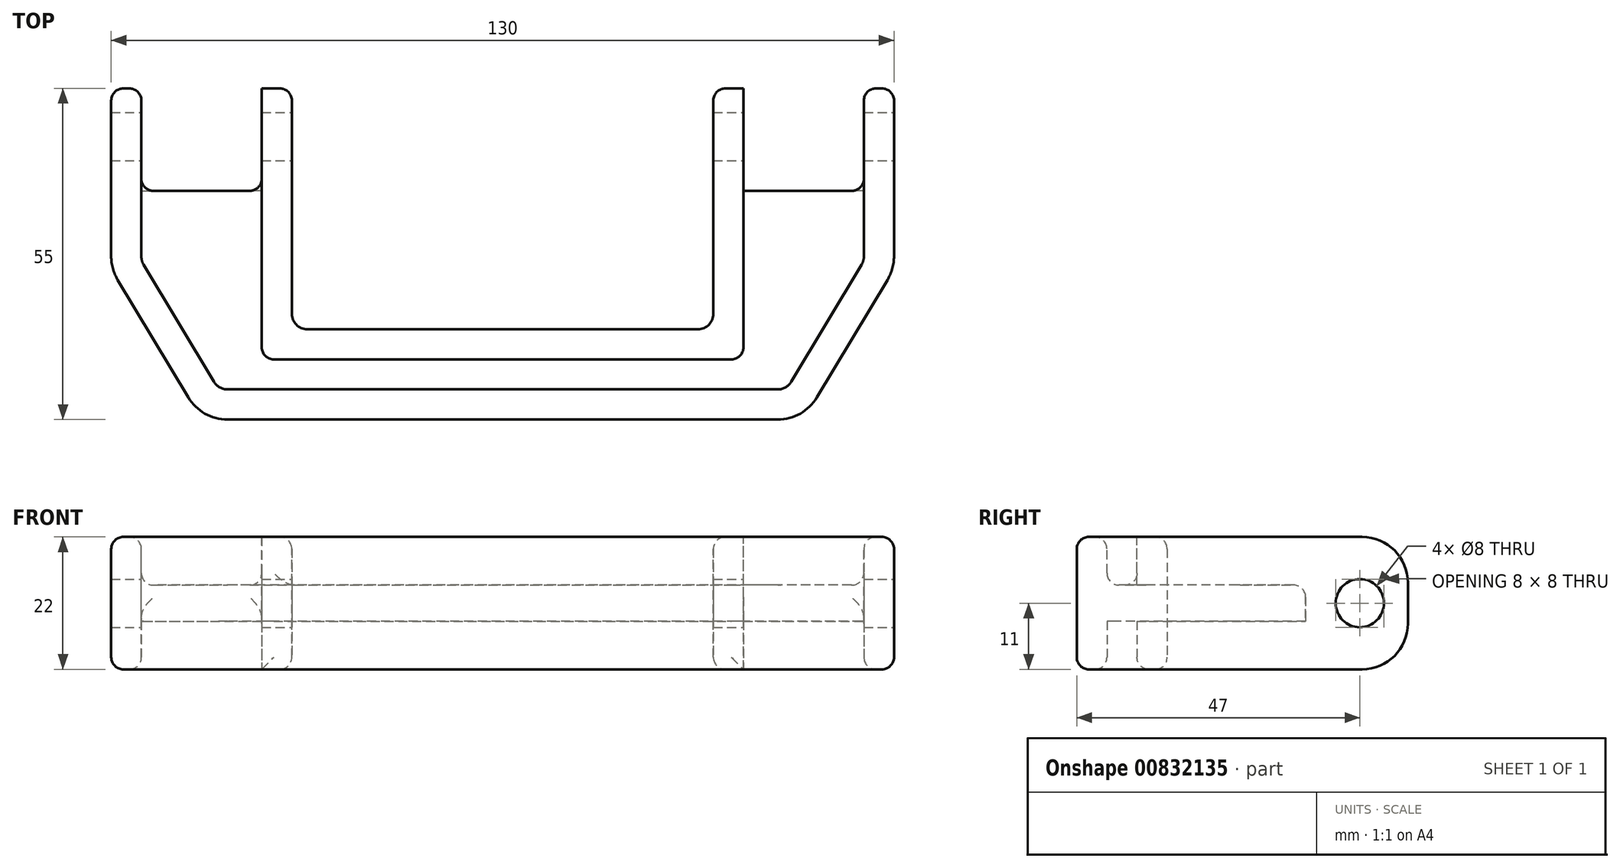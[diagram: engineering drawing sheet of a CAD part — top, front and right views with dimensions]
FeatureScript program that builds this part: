
annotation { "Feature Type Name" : "Feature", "Feature Type Description" : "" }
export const myFeature = defineFeature(function(context is Context, id is Id, definition is map)
    precondition{}
    {
        {
            var Q0;
            Q0=qCreatedBy(makeId("Top.planeOp"),FACE);
            var sketch = newSketch(context, id + "F0", { "sketchPlane" : qUnion([Q0])});
            skLineSegment(sketch, "E0", {"start": v(-65, 30) * mm, "end": v(-35, 30) * mm});
            skLineSegment(sketch, "E1", {"start": v(-35, 30) * mm, "end": v(-35, -10) * mm});
            skLineSegment(sketch, "E2", {"start": v(0, 0) * mm, "end": v(0, -25) * mm});
            skLineSegment(sketch, "E3", {"start": v(65, 30) * mm, "end": v(35, 30) * mm});
            skLineSegment(sketch, "E4", {"start": v(35, 30) * mm, "end": v(35, -10) * mm});
            skLineSegment(sketch, "E5", {"start": v(-35, -10) * mm, "end": v(35, -10) * mm});
            skLineSegment(sketch, "E6", {"start": v(0, -25) * mm, "end": v(-50, -25) * mm});
            skLineSegment(sketch, "E7", {"start": v(0, -25) * mm, "end": v(50, -25) * mm});
            skLineSegment(sketch, "E8", {"start": v(65, 30) * mm, "end": v(65, 0) * mm});
            skLineSegment(sketch, "E9", {"start": v(65, 0) * mm, "end": v(50, -25) * mm});
            skLineSegment(sketch, "E10", {"start": v(-65, 30) * mm, "end": v(-65, 0) * mm});
            skLineSegment(sketch, "E11", {"start": v(-65, 0) * mm, "end": v(-50, -25) * mm});
            skSolve(sketch);
        }
        {
            var Q0;
            Q0 = qSketchRegion(id + "F0", true);
            extrude(context, id + "F1", {"entities" : qUnion([Q0]), "depth" : 22 * mm, "offsetDistance" : 25.4 * mm});
        }
        {
            var Q0;
            Q0=makeQuery(id+"F1.opExtrude","SWEPT_EDGE",EDGE,{"disambiguationData":[OSD([sQuery(id+"F0.wireOp",EDGE,"E7"),sQuery(id+"F0.wireOp",EDGE,"E9")])]});
            var Q1;
            Q1=makeQuery(id+"F1.opExtrude","SWEPT_EDGE",EDGE,{"disambiguationData":[OSD([sQuery(id+"F0.wireOp",EDGE,"E8"),sQuery(id+"F0.wireOp",EDGE,"E9")])]});
            var Q2;
            Q2=makeQuery(id+"F1.opExtrude","SWEPT_EDGE",EDGE,{"disambiguationData":[OSD([sQuery(id+"F0.wireOp",EDGE,"E6"),sQuery(id+"F0.wireOp",EDGE,"E11")])]});
            var Q3;
            Q3=makeQuery(id+"F1.opExtrude","SWEPT_EDGE",EDGE,{"disambiguationData":[OSD([sQuery(id+"F0.wireOp",EDGE,"E10"),sQuery(id+"F0.wireOp",EDGE,"E11")])]});
            fillet(context, id + "F2", {"entities" : qUnion([Q0, Q1, Q2, Q3]), "radius" : 7.62 * mm, "tangentPropagation" : true, "allowEdgeOverflow" : false});
        }
        {
            var Q0;
            Q0=makeQuery(id+"F1.opExtrude","SWEPT_EDGE",EDGE,{"disambiguationData":[OSD([sQuery(id+"F0.wireOp",EDGE,"E4"),sQuery(id+"F0.wireOp",EDGE,"E5")])]});
            var Q1;
            Q1=makeQuery(id+"F1.opExtrude","SWEPT_EDGE",EDGE,{"disambiguationData":[OSD([sQuery(id+"F0.wireOp",EDGE,"E1"),sQuery(id+"F0.wireOp",EDGE,"E5")])]});
            fillet(context, id + "F3", {"entities" : qUnion([Q0, Q1]), "radius" : 2.54 * mm, "tangentPropagation" : true, "allowEdgeOverflow" : false});
        }
        {
            var Q0;
            Q0=makeQuery(id+"F1.opExtrude","CAP_FACE",FACE,{"disambiguationData":[OSD([sQuery(id+"F0.wireOp",EDGE,"E0"),sQuery(id+"F0.wireOp",EDGE,"E1"),sQuery(id+"F0.wireOp",EDGE,"E3"),sQuery(id+"F0.wireOp",EDGE,"E4"),sQuery(id+"F0.wireOp",EDGE,"E5"),sQuery(id+"F0.wireOp",EDGE,"E6"),sQuery(id+"F0.wireOp",EDGE,"E7"),sQuery(id+"F0.wireOp",EDGE,"E8"),sQuery(id+"F0.wireOp",EDGE,"E9"),sQuery(id+"F0.wireOp",EDGE,"E10"),sQuery(id+"F0.wireOp",EDGE,"E11")])],"isStart":false});
            var sketch = newSketch(context, id + "F4", { "sketchPlane" : qUnion([Q0])});
            skLineSegment(sketch, "E12.1", {"start": v(60, 25) * mm, "end": v(60, 2.11) * mm});
            skArc(sketch, "E12.2", {"start": v(59.63, 0.76) * mm, "mid": v(59.9, 1.41) * mm, "end": v(60, 2.11) * mm});
            skLineSegment(sketch, "E12.3", {"start": v(59.63, 0.76) * mm, "end": v(47.93, -18.73) * mm});
            skArc(sketch, "E12.4", {"start": v(45.69, -20) * mm, "mid": v(46.98, -19.66) * mm, "end": v(47.93, -18.73) * mm});
            skLineSegment(sketch, "E12.5", {"start": v(-40, 25) * mm, "end": v(-40, -7.46) * mm});
            skLineSegment(sketch, "E12.7", {"start": v(-32.46, -15) * mm, "end": v(32.46, -15) * mm});
            skLineSegment(sketch, "E12.10", {"start": v(-60, 25) * mm, "end": v(-60, 2.11) * mm});
            skArc(sketch, "E12.11", {"start": v(-60, 2.11) * mm, "mid": v(-59.9, 1.41) * mm, "end": v(-59.63, 0.76) * mm});
            skLineSegment(sketch, "E12.12", {"start": v(-59.63, 0.76) * mm, "end": v(-47.93, -18.73) * mm});
            skArc(sketch, "E12.13", {"start": v(-47.93, -18.73) * mm, "mid": v(-46.98, -19.66) * mm, "end": v(-45.69, -20) * mm});
            skLineSegment(sketch, "E12.14", {"start": v(40, 25) * mm, "end": v(40, -7.46) * mm});
            skLineSegment(sketch, "E12.15", {"start": v(45.69, -20) * mm, "end": v(-45.69, -20) * mm});
            skLineSegment(sketch, "E13", {"start": v(-40, -7.46) * mm, "end": v(-40, -15) * mm});
            skLineSegment(sketch, "E14", {"start": v(-40, -15) * mm, "end": v(-32.46, -15) * mm});
            skLineSegment(sketch, "E15", {"start": v(32.46, -15) * mm, "end": v(40, -15) * mm});
            skLineSegment(sketch, "E16", {"start": v(40, -15) * mm, "end": v(40, -7.46) * mm});
            skLineSegment(sketch, "E17", {"start": v(40, 25) * mm, "end": v(40, 30) * mm});
            skLineSegment(sketch, "E18", {"start": v(40, 30) * mm, "end": v(60, 30) * mm});
            skLineSegment(sketch, "E19", {"start": v(60, 30) * mm, "end": v(60, 25) * mm});
            skLineSegment(sketch, "E20", {"start": v(-60, 25) * mm, "end": v(-60, 30) * mm});
            skLineSegment(sketch, "E21", {"start": v(-60, 30) * mm, "end": v(-40, 30) * mm});
            skLineSegment(sketch, "E22", {"start": v(-40, 30) * mm, "end": v(-40, 25) * mm});
            skSolve(sketch);
        }
        {
            var Q0;
            Q0=makeQuery(id+"F1.opExtrude","CAP_EDGE",EDGE,{"disambiguationData":[OSD([sQuery(id+"F0.wireOp",EDGE,"E3")])],"isStart":false});
            var Q1;
            Q1=makeQuery(id+"F1.opExtrude","CAP_EDGE",EDGE,{"disambiguationData":[OSD([sQuery(id+"F0.wireOp",EDGE,"E3")])],"isStart":true});
            var Q2;
            Q2=makeQuery(id+"F1.opExtrude","CAP_EDGE",EDGE,{"disambiguationData":[OSD([sQuery(id+"F0.wireOp",EDGE,"E0")])],"isStart":false});
            var Q3;
            Q3=makeQuery(id+"F1.opExtrude","CAP_EDGE",EDGE,{"disambiguationData":[OSD([sQuery(id+"F0.wireOp",EDGE,"E0")])],"isStart":true});
            fillet(context, id + "F5", {"entities" : qUnion([Q0, Q1, Q2, Q3]), "radius" : 7.62 * mm, "tangentPropagation" : true, "allowEdgeOverflow" : false});
        }
        {
            var Q0;
            Q0 = qSketchRegion(id + "F4", true);
            extrude(context, id + "F6", {"entities" : qUnion([Q0]), "operationType" : NewBodyOperationType.REMOVE, "oppositeDirection" : true, "depth" : 8 * mm, "offsetDistance" : 25.4 * mm});
        }
        {
            var Q0;
            Q0=makeQuery(id+"F1.opExtrude","CAP_FACE",FACE,{"disambiguationData":[OSD([sQuery(id+"F0.wireOp",EDGE,"E0"),sQuery(id+"F0.wireOp",EDGE,"E1"),sQuery(id+"F0.wireOp",EDGE,"E3"),sQuery(id+"F0.wireOp",EDGE,"E4"),sQuery(id+"F0.wireOp",EDGE,"E5"),sQuery(id+"F0.wireOp",EDGE,"E6"),sQuery(id+"F0.wireOp",EDGE,"E7"),sQuery(id+"F0.wireOp",EDGE,"E8"),sQuery(id+"F0.wireOp",EDGE,"E9"),sQuery(id+"F0.wireOp",EDGE,"E10"),sQuery(id+"F0.wireOp",EDGE,"E11")])],"isStart":true});
            var sketch = newSketch(context, id + "F7", { "sketchPlane" : qUnion([Q0])});
            skLineSegment(sketch, "E23.0", {"start": v(60, -22.38) * mm, "end": v(60, -2.11) * mm});
            skArc(sketch, "E23.1", {"start": v(60, -2.11) * mm, "mid": v(59.9, -1.41) * mm, "end": v(59.63, -0.76) * mm});
            skLineSegment(sketch, "E23.2", {"start": v(59.63, -0.76) * mm, "end": v(47.93, 18.73) * mm});
            skArc(sketch, "E23.3", {"start": v(47.93, 18.73) * mm, "mid": v(46.98, 19.66) * mm, "end": v(45.69, 20) * mm});
            skLineSegment(sketch, "E23.4", {"start": v(45.69, 20) * mm, "end": v(-45.69, 20) * mm});
            skLineSegment(sketch, "E23.6", {"start": v(-32.46, 15) * mm, "end": v(32.46, 15) * mm});
            skLineSegment(sketch, "E23.8", {"start": v(40, -22.38) * mm, "end": v(40, 7.46) * mm});
            skLineSegment(sketch, "E23.9", {"start": v(-40, -17.38) * mm, "end": v(-40, 7.46) * mm});
            skLineSegment(sketch, "E23.11", {"start": v(-60, -17.38) * mm, "end": v(-60, -2.11) * mm});
            skArc(sketch, "E23.12", {"start": v(-59.63, -0.76) * mm, "mid": v(-59.9, -1.41) * mm, "end": v(-60, -2.11) * mm});
            skLineSegment(sketch, "E23.13", {"start": v(-59.63, -0.76) * mm, "end": v(-47.93, 18.73) * mm});
            skArc(sketch, "E23.14", {"start": v(-45.69, 20) * mm, "mid": v(-46.98, 19.66) * mm, "end": v(-47.93, 18.73) * mm});
            skLineSegment(sketch, "E24", {"start": v(40, 7.46) * mm, "end": v(40, 15) * mm});
            skLineSegment(sketch, "E25", {"start": v(40, 15) * mm, "end": v(32.46, 15) * mm});
            skLineSegment(sketch, "E26", {"start": v(-40, 7.46) * mm, "end": v(-40, 15) * mm});
            skLineSegment(sketch, "E27", {"start": v(-40, 15) * mm, "end": v(-32.46, 15) * mm});
            skLineSegment(sketch, "E28", {"start": v(-40, -17.38) * mm, "end": v(-40, -32.17) * mm});
            skLineSegment(sketch, "E29", {"start": v(-40, -32.17) * mm, "end": v(-60, -32.17) * mm});
            skLineSegment(sketch, "E30", {"start": v(-60, -32.17) * mm, "end": v(-60, -17.38) * mm});
            skLineSegment(sketch, "E31", {"start": v(60, -22.38) * mm, "end": v(60, -34.16) * mm});
            skLineSegment(sketch, "E32", {"start": v(60, -34.16) * mm, "end": v(40, -34.16) * mm});
            skLineSegment(sketch, "E33", {"start": v(40, -34.16) * mm, "end": v(40, -22.38) * mm});
            skSolve(sketch);
        }
        {
            var Q0;
            Q0 = qSketchRegion(id + "F7", true);
            extrude(context, id + "F8", {"entities" : qUnion([Q0]), "operationType" : NewBodyOperationType.REMOVE, "oppositeDirection" : true, "depth" : 8 * mm, "offsetDistance" : 25.4 * mm});
        }
        {
            var Q0;
            Q0=makeQuery(id+"F8.boolean.opBoolean","COPY",FACE,{"derivedFrom":makeQuery(id+"F8.opExtrude","CAP_FACE",FACE,{"disambiguationData":[OSD([sQuery(id+"F7.wireOp",EDGE,"E23.0"),sQuery(id+"F7.wireOp",EDGE,"E23.1"),sQuery(id+"F7.wireOp",EDGE,"E23.2"),sQuery(id+"F7.wireOp",EDGE,"E23.3"),sQuery(id+"F7.wireOp",EDGE,"E23.4"),sQuery(id+"F7.wireOp",EDGE,"E23.6"),sQuery(id+"F7.wireOp",EDGE,"E23.8"),sQuery(id+"F7.wireOp",EDGE,"E23.9"),sQuery(id+"F7.wireOp",EDGE,"E23.11"),sQuery(id+"F7.wireOp",EDGE,"E23.12"),sQuery(id+"F7.wireOp",EDGE,"E23.13"),sQuery(id+"F7.wireOp",EDGE,"E23.14"),sQuery(id+"F7.wireOp",EDGE,"E24"),sQuery(id+"F7.wireOp",EDGE,"E25"),sQuery(id+"F7.wireOp",EDGE,"E26"),sQuery(id+"F7.wireOp",EDGE,"E27"),sQuery(id+"F7.wireOp",EDGE,"E28"),sQuery(id+"F7.wireOp",EDGE,"E29"),sQuery(id+"F7.wireOp",EDGE,"E30"),sQuery(id+"F7.wireOp",EDGE,"E31"),sQuery(id+"F7.wireOp",EDGE,"E32"),sQuery(id+"F7.wireOp",EDGE,"E33")])],"isStart":false})});
            var sketch = newSketch(context, id + "F9", { "sketchPlane" : qUnion([Q0])});
            skLineSegment(sketch, "E34", {"start": v(-40, -30) * mm, "end": v(-60, -30) * mm});
            skLineSegment(sketch, "E35", {"start": v(-60, -30) * mm, "end": v(-60, -13) * mm});
            skLineSegment(sketch, "E36", {"start": v(-60, -13) * mm, "end": v(-40, -13) * mm});
            skLineSegment(sketch, "E37", {"start": v(-40, -13) * mm, "end": v(-40, -30) * mm});
            skLineSegment(sketch, "E38", {"start": v(40, -30) * mm, "end": v(60, -30) * mm});
            skLineSegment(sketch, "E39", {"start": v(40, -13) * mm, "end": v(40, -30) * mm});
            skLineSegment(sketch, "E40", {"start": v(40, -13) * mm, "end": v(60, -13) * mm});
            skLineSegment(sketch, "E41", {"start": v(60, -13) * mm, "end": v(60, -30) * mm});
            skSolve(sketch);
        }
        {
            var Q0;
            Q0 = qSketchRegion(id + "F9", true);
            extrude(context, id + "F10", {"entities" : qUnion([Q0]), "operationType" : NewBodyOperationType.REMOVE, "oppositeDirection" : true, "depth" : 25.4 * mm, "offsetDistance" : 25.4 * mm});
        }
        {
            var Q0;
            Q0=makeQuery(id+"F6.boolean.opBoolean","COPY",EDGE,{"derivedFrom":makeQuery(id+"F6.opExtrude","CAP_EDGE",EDGE,{"disambiguationData":[OSD([sQuery(id+"F4.wireOp",EDGE,"E12.10"),sQuery(id+"F4.wireOp",EDGE,"E20")])],"isStart":true})});
            var Q1;
            Q1=makeQuery(id+"F6.boolean.opBoolean","COPY",EDGE,{"derivedFrom":makeQuery(id+"F6.opExtrude","CAP_EDGE",EDGE,{"disambiguationData":[OSD([sQuery(id+"F4.wireOp",EDGE,"E12.7"),sQuery(id+"F4.wireOp",EDGE,"E14"),sQuery(id+"F4.wireOp",EDGE,"E15")])],"isStart":true})});
            var Q2;
            Q2=makeQuery(id+"F6.boolean.opBoolean","COPY",EDGE,{"derivedFrom":makeQuery(id+"F6.opExtrude","CAP_EDGE",EDGE,{"disambiguationData":[OSD([sQuery(id+"F4.wireOp",EDGE,"E12.5"),sQuery(id+"F4.wireOp",EDGE,"E13"),sQuery(id+"F4.wireOp",EDGE,"E22")])],"isStart":true})});
            var Q3;
            Q3=makeQuery(id+"F6.boolean.opBoolean","COPY",EDGE,{"derivedFrom":makeQuery(id+"F6.opExtrude","CAP_EDGE",EDGE,{"disambiguationData":[OSD([sQuery(id+"F4.wireOp",EDGE,"E12.14"),sQuery(id+"F4.wireOp",EDGE,"E16"),sQuery(id+"F4.wireOp",EDGE,"E17")])],"isStart":true})});
            var Q4;
            Q4=makeQuery(id+"F6.boolean.opBoolean","COPY",EDGE,{"derivedFrom":makeQuery(id+"F6.opExtrude","SWEPT_EDGE",EDGE,{"disambiguationData":[OSD([sQuery(id+"F4.wireOp",EDGE,"E15"),sQuery(id+"F4.wireOp",EDGE,"E16")])]})});
            var Q5;
            Q5=makeQuery(id+"F6.boolean.opBoolean","COPY",EDGE,{"derivedFrom":makeQuery(id+"F6.opExtrude","SWEPT_EDGE",EDGE,{"disambiguationData":[OSD([sQuery(id+"F4.wireOp",EDGE,"E13"),sQuery(id+"F4.wireOp",EDGE,"E14")])]})});
            var Q6;
            Q6=makeQuery(id+"F1.opExtrude","CAP_EDGE",EDGE,{"disambiguationData":[OSD([sQuery(id+"F0.wireOp",EDGE,"E5")])],"isStart":false});
            var Q7;
            Q7=makeQuery(id+"F1.opExtrude","CAP_EDGE",EDGE,{"disambiguationData":[OSD([sQuery(id+"F0.wireOp",EDGE,"E6"),sQuery(id+"F0.wireOp",EDGE,"E7")])],"isStart":false});
            var Q8;
            Q8=makeQuery(id+"F6.boolean.opBoolean","COPY",EDGE,{"derivedFrom":makeQuery(id+"F6.opExtrude","CAP_EDGE",EDGE,{"disambiguationData":[OSD([sQuery(id+"F4.wireOp",EDGE,"E12.15")])],"isStart":false})});
            var Q9;
            Q9=makeQuery(id+"F6.boolean.opBoolean","COPY",EDGE,{"derivedFrom":makeQuery(id+"F6.opExtrude","CAP_EDGE",EDGE,{"disambiguationData":[OSD([sQuery(id+"F4.wireOp",EDGE,"E12.5"),sQuery(id+"F4.wireOp",EDGE,"E13"),sQuery(id+"F4.wireOp",EDGE,"E22")])],"isStart":false})});
            var Q10;
            Q10=makeQuery(id+"F10.boolean.opBoolean","INTERSECT",EDGE,{"derivedFrom":[makeQuery(id+"F6.boolean.opBoolean","COPY",FACE,{"derivedFrom":makeQuery(id+"F6.opExtrude","CAP_FACE",FACE,{"disambiguationData":[OSD([sQuery(id+"F4.wireOp",EDGE,"E12.1"),sQuery(id+"F4.wireOp",EDGE,"E12.2"),sQuery(id+"F4.wireOp",EDGE,"E12.3"),sQuery(id+"F4.wireOp",EDGE,"E12.4"),sQuery(id+"F4.wireOp",EDGE,"E12.5"),sQuery(id+"F4.wireOp",EDGE,"E12.7"),sQuery(id+"F4.wireOp",EDGE,"E12.10"),sQuery(id+"F4.wireOp",EDGE,"E12.11"),sQuery(id+"F4.wireOp",EDGE,"E12.12"),sQuery(id+"F4.wireOp",EDGE,"E12.13"),sQuery(id+"F4.wireOp",EDGE,"E12.14"),sQuery(id+"F4.wireOp",EDGE,"E12.15"),sQuery(id+"F4.wireOp",EDGE,"E13"),sQuery(id+"F4.wireOp",EDGE,"E14"),sQuery(id+"F4.wireOp",EDGE,"E15"),sQuery(id+"F4.wireOp",EDGE,"E16"),sQuery(id+"F4.wireOp",EDGE,"E17"),sQuery(id+"F4.wireOp",EDGE,"E18"),sQuery(id+"F4.wireOp",EDGE,"E19"),sQuery(id+"F4.wireOp",EDGE,"E20"),sQuery(id+"F4.wireOp",EDGE,"E21"),sQuery(id+"F4.wireOp",EDGE,"E22")])],"isStart":false})}),makeQuery(id+"F10.opExtrude","SWEPT_FACE",FACE,{"disambiguationData":[OSD([sQuery(id+"F9.wireOp",EDGE,"E40")])]})]});
            var Q11;
            Q11=makeQuery(id+"F10.boolean.opBoolean","COPY",EDGE,{"derivedFrom":makeQuery(id+"F10.opExtrude","CAP_EDGE",EDGE,{"disambiguationData":[OSD([sQuery(id+"F9.wireOp",EDGE,"E40")])],"isStart":true})});
            var Q12;
            Q12=makeQuery(id+"F10.boolean.opBoolean","INTERSECT",EDGE,{"derivedFrom":[makeQuery(id+"F6.boolean.opBoolean","COPY",FACE,{"derivedFrom":makeQuery(id+"F6.opExtrude","CAP_FACE",FACE,{"disambiguationData":[OSD([sQuery(id+"F4.wireOp",EDGE,"E12.1"),sQuery(id+"F4.wireOp",EDGE,"E12.2"),sQuery(id+"F4.wireOp",EDGE,"E12.3"),sQuery(id+"F4.wireOp",EDGE,"E12.4"),sQuery(id+"F4.wireOp",EDGE,"E12.5"),sQuery(id+"F4.wireOp",EDGE,"E12.7"),sQuery(id+"F4.wireOp",EDGE,"E12.10"),sQuery(id+"F4.wireOp",EDGE,"E12.11"),sQuery(id+"F4.wireOp",EDGE,"E12.12"),sQuery(id+"F4.wireOp",EDGE,"E12.13"),sQuery(id+"F4.wireOp",EDGE,"E12.14"),sQuery(id+"F4.wireOp",EDGE,"E12.15"),sQuery(id+"F4.wireOp",EDGE,"E13"),sQuery(id+"F4.wireOp",EDGE,"E14"),sQuery(id+"F4.wireOp",EDGE,"E15"),sQuery(id+"F4.wireOp",EDGE,"E16"),sQuery(id+"F4.wireOp",EDGE,"E17"),sQuery(id+"F4.wireOp",EDGE,"E18"),sQuery(id+"F4.wireOp",EDGE,"E19"),sQuery(id+"F4.wireOp",EDGE,"E20"),sQuery(id+"F4.wireOp",EDGE,"E21"),sQuery(id+"F4.wireOp",EDGE,"E22")])],"isStart":false})}),makeQuery(id+"F10.opExtrude","SWEPT_FACE",FACE,{"disambiguationData":[OSD([sQuery(id+"F9.wireOp",EDGE,"E36")])]})]});
            var Q13;
            Q13=makeQuery(id+"F10.boolean.opBoolean","COPY",EDGE,{"derivedFrom":makeQuery(id+"F10.opExtrude","CAP_EDGE",EDGE,{"disambiguationData":[OSD([sQuery(id+"F9.wireOp",EDGE,"E36")])],"isStart":true})});
            var Q14;
            Q14=makeQuery(id+"F8.boolean.opBoolean","COPY",EDGE,{"derivedFrom":makeQuery(id+"F8.opExtrude","SWEPT_EDGE",EDGE,{"disambiguationData":[OSD([sQuery(id+"F7.wireOp",EDGE,"E26"),sQuery(id+"F7.wireOp",EDGE,"E27")])]})});
            var Q15;
            Q15=makeQuery(id+"F8.boolean.opBoolean","COPY",EDGE,{"derivedFrom":makeQuery(id+"F8.opExtrude","CAP_EDGE",EDGE,{"disambiguationData":[OSD([sQuery(id+"F7.wireOp",EDGE,"E23.6"),sQuery(id+"F7.wireOp",EDGE,"E25"),sQuery(id+"F7.wireOp",EDGE,"E27")])],"isStart":true})});
            var Q16;
            Q16=makeQuery(id+"F8.boolean.opBoolean","COPY",EDGE,{"derivedFrom":makeQuery(id+"F8.opExtrude","SWEPT_EDGE",EDGE,{"disambiguationData":[OSD([sQuery(id+"F7.wireOp",EDGE,"E24"),sQuery(id+"F7.wireOp",EDGE,"E25")])]})});
            fillet(context, id + "F11", {"entities" : qUnion([Q0, Q1, Q2, Q3, Q4, Q5, Q6, Q7, Q8, Q9, Q10, Q11, Q12, Q13, Q14, Q15, Q16]), "radius" : 2 * mm, "tangentPropagation" : true, "allowEdgeOverflow" : false});
        }
        {
            var Q0;
            Q0=makeQuery(id+"F1.opExtrude","SWEPT_FACE",FACE,{"disambiguationData":[OSD([sQuery(id+"F0.wireOp",EDGE,"E8")])]});
            var sketch = newSketch(context, id + "F12", { "sketchPlane" : qUnion([Q0])});
            skLineSegment(sketch, "E42", {"start": v(28, 11) * mm, "end": v(22, 11) * mm});
            skCircle(sketch, "E43", {"center": v(22, 11) * mm, "radius": 4 * mm});
            skSolve(sketch);
        }
        {
            var Q0;
            Q0=makeQuery(id+"F12.imprint","IMPRINT",FACE,{"disambiguationData":[TD([[makeQuery(id+"F12.imprint","IMPRINT",EDGE,{"derivedFrom":sQuery(id+"F12.wireOp",EDGE,"E43")}),1.0]])]});
            extrude(context, id + "F13", {"entities" : qUnion([Q0]), "operationType" : NewBodyOperationType.REMOVE, "oppositeDirection" : true, "depth" : 143 * mm, "offsetDistance" : 25.4 * mm});
        }
    });
